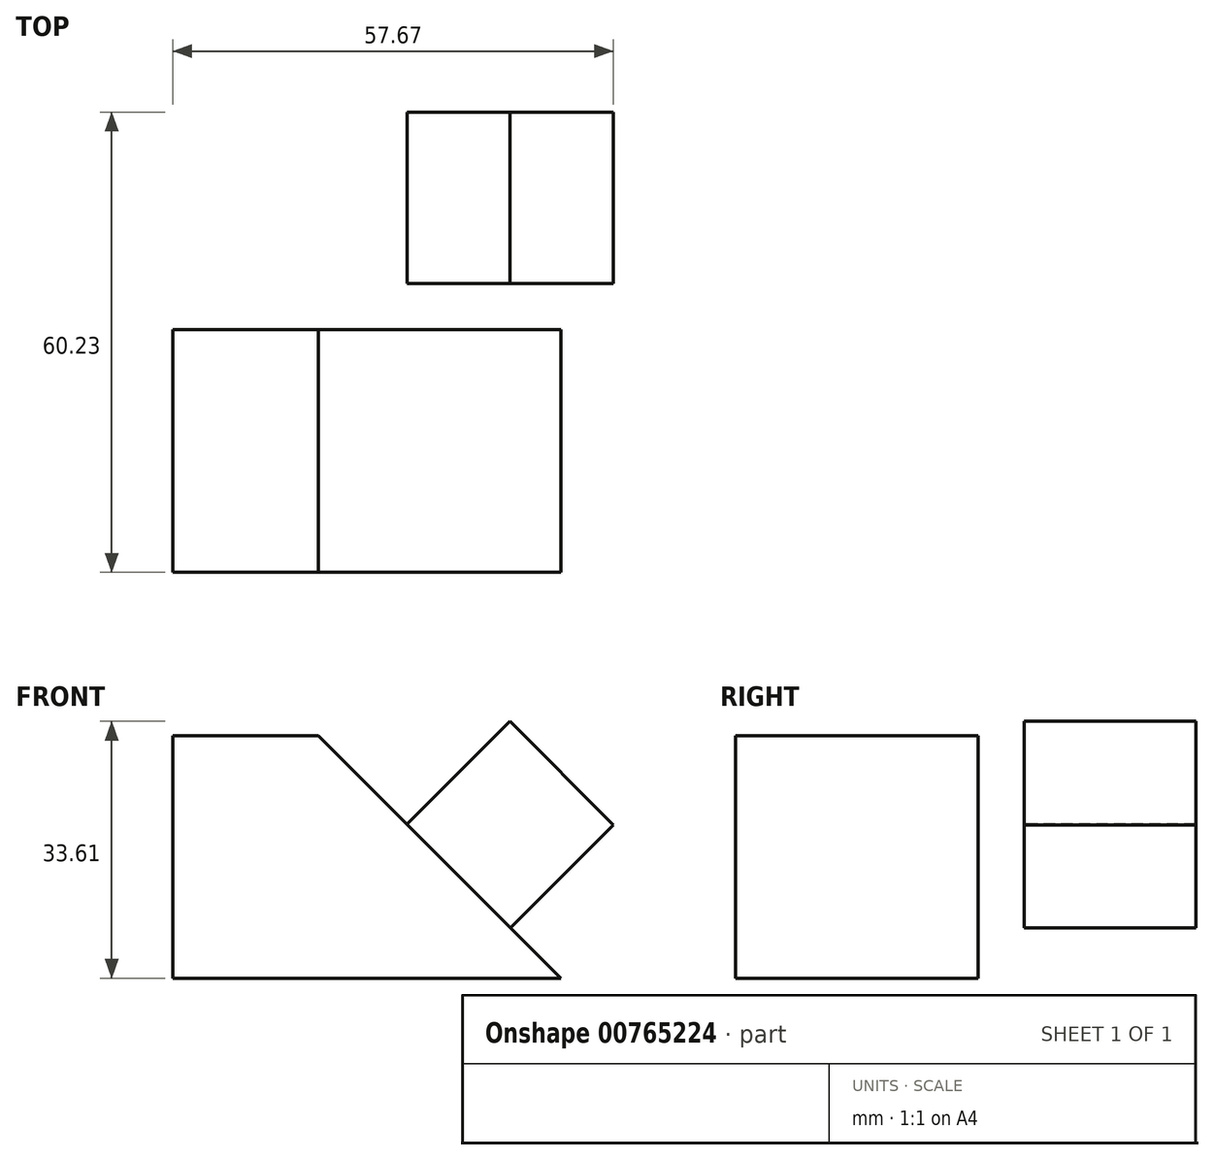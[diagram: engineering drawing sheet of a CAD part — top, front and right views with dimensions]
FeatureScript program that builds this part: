
annotation { "Feature Type Name" : "Feature", "Feature Type Description" : "" }
export const myFeature = defineFeature(function(context is Context, id is Id, definition is map)
    precondition{}
    {
        {
            var Q0;
            Q0=qCreatedBy(makeId("Front.planeOp"),FACE);
            var sketch = newSketch(context, id + "F0", { "sketchPlane" : qUnion([Q0])});
            skLineSegment(sketch, "E0", {"start": v(-12.93, 29.34) * mm, "end": v(6.12, 29.34) * mm});
            skLineSegment(sketch, "E1", {"start": v(-12.93, 29.34) * mm, "end": v(-12.93, -2.41) * mm});
            skLineSegment(sketch, "E2", {"start": v(-12.93, -2.41) * mm, "end": v(37.87, -2.41) * mm});
            skLineSegment(sketch, "E3", {"start": v(6.12, 29.34) * mm, "end": v(37.87, -2.41) * mm});
            skSolve(sketch);
        }
        {
            var Q0;
            Q0=makeQuery(id+"F0.imprint","IMPRINT",FACE,{"disambiguationData":[TD([[makeQuery(id+"F0.imprint","IMPRINT",EDGE,{"derivedFrom":sQuery(id+"F0.wireOp",EDGE,"E0")}),-1.0]])]});
            extrude(context, id + "F1", {"entities" : qUnion([Q0]), "depth" : 31.75 * mm, "offsetDistance" : 25.4 * mm});
        }
        {
            var Q0;
            Q0=makeQuery(id+"F1.opExtrude","SWEPT_FACE",FACE,{"disambiguationData":[OSD([sQuery(id+"F0.wireOp",EDGE,"E3")])]});
            var sketch = newSketch(context, id + "F2", { "sketchPlane" : qUnion([Q0])});
            skLineSegment(sketch, "E4", {"start": v(28.48, 0) * mm, "end": v(0, 0) * mm});
            skLineSegment(sketch, "E5", {"start": v(6.03, 0) * mm, "end": v(6.03, -19.15) * mm});
            skLineSegment(sketch, "E6", {"start": v(6.03, -19.15) * mm, "end": v(28.48, -19.15) * mm});
            skLineSegment(sketch, "E7", {"start": v(28.48, -19.15) * mm, "end": v(28.48, 0) * mm});
            skSolve(sketch);
        }
        {
            var Q0;
            {var subQ2=sQuery(id+"F2.wireOp",EDGE,"E5");Q0=makeQuery(id+"F2.imprint","IMPRINT",FACE,{"disambiguationData":[TD([[makeQuery(id+"F2.imprint","IMPRINT",EDGE,{"derivedFrom":subQ2}),1.0]])]});}
            extrude(context, id + "F3", {"entities" : qUnion([Q0]), "depth" : 19.05 * mm, "offsetDistance" : 25.4 * mm});
        }
    });
